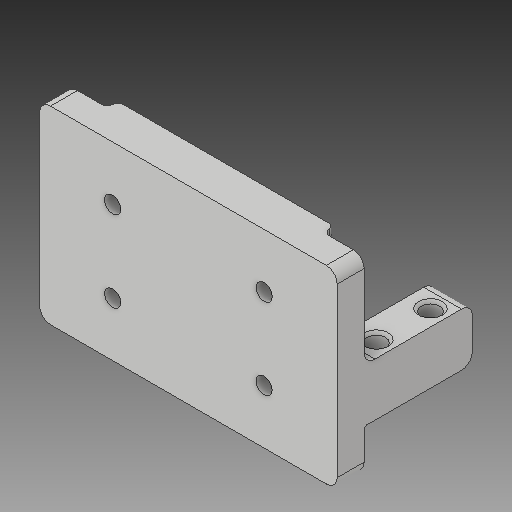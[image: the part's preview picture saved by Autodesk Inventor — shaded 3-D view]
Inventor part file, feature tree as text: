
AUTODESK INVENTOR PART (.ipt)
format: ipt  version: 2019 (Build 230136000, 136)  size: 202,752 bytes
history: native  units: mm
features: sketch x4, other x3
ambient origin geometry x8: Origin, YZ Plane, XZ Plane, XY Plane, X Axis, Y Axis, Z Axis, Center Point
bodies: Solid1 (feature_tree)
feature tree (7):
  other  "big_servo_hold.ipt"
  other  "Solid1::big_servo_hold.ipt"
  other  "TaggingFeature1"
  sketch  "Sketch1"  dims[d0=10.0mm]
  sketch  "Sketch2"
  sketch  "Sketch3"
  sketch  "Sketch4"
